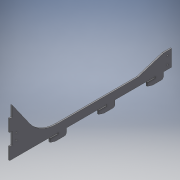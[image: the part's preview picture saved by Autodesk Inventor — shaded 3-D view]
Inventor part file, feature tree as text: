
AUTODESK INVENTOR PART (.ipt)
format: ipt  version: 2017 (Build 210142000, 142)  size: 173,056 bytes
history: native  units: mm
features: sketch x2, extrude x1, hole x1
ambient origin geometry x8: Origin, YZ Plane, XZ Plane, XY Plane, X Axis, Y Axis, Z Axis, Center Point
bodies: Solid1 (feature_tree)
feature tree (4):
  extrude  "Extrusion1"  Depth=40.0mm
  hole  "Hole1"  [1 undecoded]
  sketch  "Sketch1"  dims[d0=400.0mm d2=40.0mm]
  sketch  "Sketch2"  dims[d3=90.0mm d4=3.0mm d5=0.0mm d6=3.0mm d7=3.0mm d8=20.0mm d9=20.0mm d10=12.0mm d11=5.0mm d12=30.0mm d14=120.0mm d15=10.0mm d17=10.0mm d19=8.0mm d20=22.0mm d21=20.0mm d22=6.0mm d23=30.0mm d24=30.0mm d25=16.0mm d26=16.0mm d27=20.0mm d28=10.0mm d29=10.0mm d30=36.0mm d31=3.2mm d32=6.0mm d33=4.0mm d34=2.0mm d35=90.0deg d36=8.0mm d37=20.594885mm]
note: 1 required parameter value undecoded (feature->parameter linkage not recoverable at this tier; creation-order binding heuristic only, values carry confidence <= 0.55)
